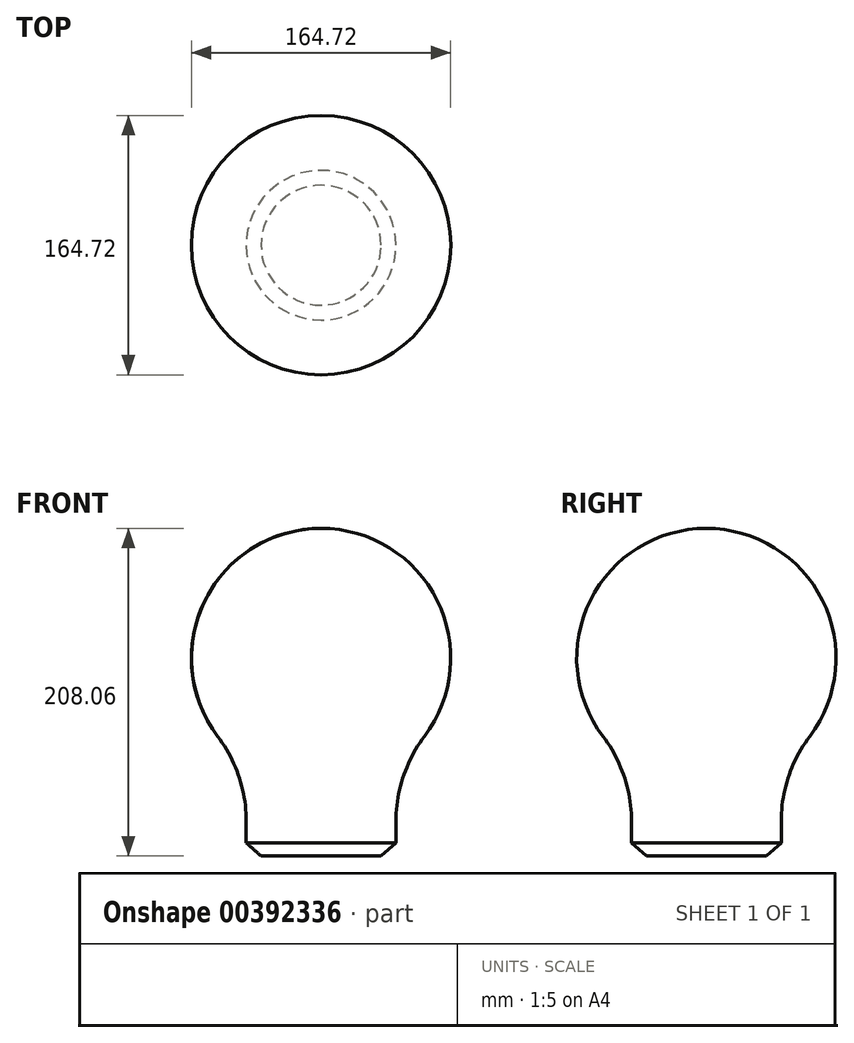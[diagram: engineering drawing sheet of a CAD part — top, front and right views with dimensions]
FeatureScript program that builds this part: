
annotation { "Feature Type Name" : "Feature", "Feature Type Description" : "" }
export const myFeature = defineFeature(function(context is Context, id is Id, definition is map)
    precondition{}
    {
        {
            var Q0;
            Q0=qCreatedBy(makeId("Front.planeOp"),FACE);
            var sketch = newSketch(context, id + "F0", { "sketchPlane" : qUnion([Q0])});
            skLineSegment(sketch, "E0", {"start": v(-38.1, 0) * mm, "end": v(-47.56, 8.38) * mm});
            skLineSegment(sketch, "E1", {"start": v(-47.56, 8.38) * mm, "end": v(-47.56, 22) * mm});
            skLineSegment(sketch, "E2", {"start": v(0, 0) * mm, "end": v(0, 208.06) * mm});
            skLineSegment(sketch, "E3", {"start": v(0, 0) * mm, "end": v(-38.1, 0) * mm});
            skArc(sketch, "E4", {"start": v(-47.56, 22) * mm, "mid": v(-52.2, 50.48) * mm, "end": v(-65.68, 76) * mm});
            skArc(sketch, "E5", {"start": v(0, 208.06) * mm, "mid": v(-73.74, 162.38) * mm, "end": v(-65.68, 76) * mm});
            skLineSegment(sketch, "E6", {"start": v(-38.1, 0) * mm, "end": v(0, 127) * mm, "construction": true});
            skLineSegment(sketch, "E7", {"start": v(0, 208.06) * mm, "end": v(87.5, 208.06) * mm, "construction": true});
            skSolve(sketch);
        }
        {
            var Q0;
            Q0=makeQuery(id+"F0.imprint","IMPRINT",FACE,{"disambiguationData":[TD([[makeQuery(id+"F0.imprint","IMPRINT",EDGE,{"derivedFrom":sQuery(id+"F0.wireOp",EDGE,"E0")}),-1.0]])]});
            var Q1;
            Q1=sQuery(id+"F0.wireOp",EDGE,"E2");
            revolve(context, id + "F1", {"surfaceOperationType" : NewSurfaceOperationType.NEW, "entities" : qUnion([Q0]), "axis" : qUnion([Q1]), "revolveType" : RevolveType.FULL});
        }
    });
